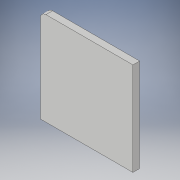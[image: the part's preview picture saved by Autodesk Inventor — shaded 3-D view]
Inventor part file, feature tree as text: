
AUTODESK INVENTOR PART (.ipt)
format: ipt  version: 2018 (Build 220112000, 112)  size: 92,672 bytes
history: native  units: in
note: dims shown in document units (in); Inventor stores cm internally (conversion verified against a paired STEP export)
features: extrude x1, fillet x1, sketch x1
ambient origin geometry x8: Origin, YZ Plane, XZ Plane, XY Plane, X Axis, Y Axis, Z Axis, Center Point
bodies: Solid1 (feature_tree)
feature tree (3):
  extrude  "Extrusion1"  Depth=2.092in
  fillet  "Fillet1"  Radius=0.15in
  sketch  "Sketch1"  dims[d0=2.079in d1=2.092in d2=0.15in d3=0.0in d4=0.125in]
